# Revit family: BuroSeating_Konfurb Hady Sled Base
name_source: partatom
category: Furniture
units: mm (PartAtom-declared; Revit-internal decimal feet)

## family parameters
Always vertical = Yes
Cut with Voids When Loaded = No
OmniClass Number = 23.40.70.14.64.11
OmniClass Title = Office Furniture
Room Calculation Point = No
Shared = No
Work Plane-Based = No

## types (1)
- KON503-B18
    Assembly Code = E2020
    BaseOffset = 18 mm  [stored 0.0590551 ft]
    Default Elevation = 0 mm  [stored 0 ft]
    Description = Konfurb Hady Sled Base
    FeetMaterial = BuroSeating_Plastic_Black
    FrameMaterial = BuroSeating_Metal_Chrome_Semi-Polished
    Manufacturer = Buro Seating
    Model = KON503-B18
    NominalDepth = 615 mm  [stored 2.01772 ft]
    NominalHeight = 855 mm  [stored 2.80512 ft]
    NominalWidth = 600 mm
    ProductGroup = Konfurb Hady
    ProductPageURL AU = https://buroseating.com
    ProductPageURL NZ = https://buroseating.co.nz
    ProductRange = Konfurb
    SeatHeight = 465 mm  [stored 1.52559 ft]
    URL = https://buroseating.co.nz
    URL AU = https://buroseating.com
    WarrantyDescription = Full 5 year guarantee (excluding upholstery)

note: [stored X ft] marks values corroborated as IEEE doubles in the binary element streams (Revit-internal decimal feet)

## geometry (parser evidence)
native form markers: Sweep x5
no freeform markers — native parametric forms only
